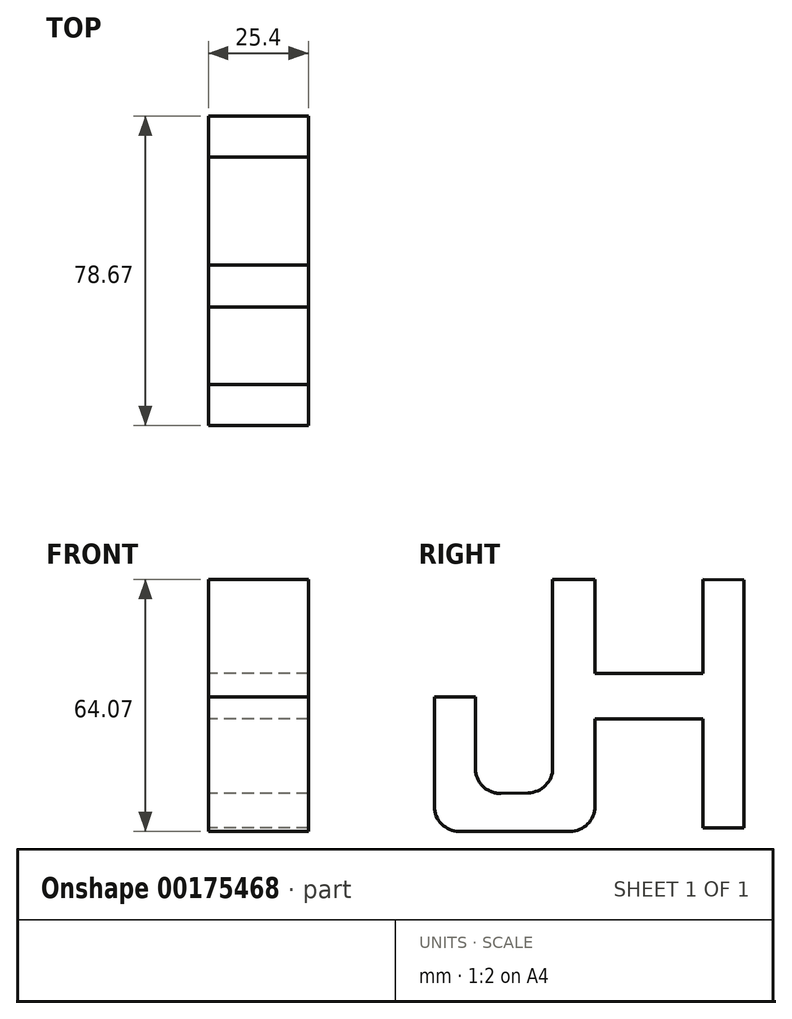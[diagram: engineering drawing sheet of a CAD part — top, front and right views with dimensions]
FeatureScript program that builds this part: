
annotation { "Feature Type Name" : "Feature", "Feature Type Description" : "" }
export const myFeature = defineFeature(function(context is Context, id is Id, definition is map)
    precondition{}
    {
        {
            var Q0;
            Q0=qCreatedBy(makeId("Right.planeOp"),FACE);
            var sketch = newSketch(context, id + "F0", { "sketchPlane" : qUnion([Q0])});
            skLineSegment(sketch, "E0", {"start": v(-25.03, 29.95) * mm, "end": v(-25.03, -17.98) * mm});
            skLineSegment(sketch, "E1", {"start": v(-25.03, 29.95) * mm, "end": v(-14.3, 29.95) * mm});
            skLineSegment(sketch, "E2", {"start": v(-14.3, 29.95) * mm, "end": v(-14.3, -27.77) * mm});
            skLineSegment(sketch, "E3", {"start": v(-20.65, -34.12) * mm, "end": v(-48.78, -34.12) * mm});
            skLineSegment(sketch, "E4", {"start": v(-55.13, -27.77) * mm, "end": v(-55.13, 0) * mm});
            skLineSegment(sketch, "E5", {"start": v(-55.13, 0) * mm, "end": v(-44.7, 0) * mm});
            skLineSegment(sketch, "E6", {"start": v(-44.7, 0) * mm, "end": v(-44.7, -18.12) * mm});
            skLineSegment(sketch, "E7", {"start": v(-38.23, -24.47) * mm, "end": v(-31.26, -24.33) * mm});
            skPoint(sketch, "E8.visualSharp", {"position": v(-44.7, -24.59) * mm});
            skArc(sketch, "E8.filletArc", {"start": v(-44.7, -18.12) * mm, "mid": v(-42.8, -22.65) * mm, "end": v(-38.23, -24.47) * mm});
            skPoint(sketch, "E9.visualSharp", {"position": v(-55.13, -34.12) * mm});
            skArc(sketch, "E9.filletArc", {"start": v(-55.13, -27.77) * mm, "mid": v(-53.27, -32.26) * mm, "end": v(-48.78, -34.12) * mm});
            skPoint(sketch, "E10.visualSharp", {"position": v(-14.3, -34.12) * mm});
            skArc(sketch, "E10.filletArc", {"start": v(-20.65, -34.12) * mm, "mid": v(-16.16, -32.26) * mm, "end": v(-14.3, -27.77) * mm});
            skPoint(sketch, "E11.visualSharp", {"position": v(-25.03, -24.21) * mm});
            skArc(sketch, "E11.filletArc", {"start": v(-31.26, -24.33) * mm, "mid": v(-26.85, -22.43) * mm, "end": v(-25.03, -17.98) * mm});
            skLineSegment(sketch, "E12", {"start": v(-14.3, 6.07) * mm, "end": v(13.11, 6.07) * mm});
            skLineSegment(sketch, "E13", {"start": v(13.11, 29.9) * mm, "end": v(13.11, 29.9) * mm});
            skLineSegment(sketch, "E14", {"start": v(13.11, 29.9) * mm, "end": v(23.54, 29.76) * mm});
            skLineSegment(sketch, "E15", {"start": v(23.54, 29.76) * mm, "end": v(23.54, -33.27) * mm});
            skLineSegment(sketch, "E16", {"start": v(23.54, -33.27) * mm, "end": v(13.11, -33.27) * mm});
            skLineSegment(sketch, "E17", {"start": v(13.11, -33.27) * mm, "end": v(13.11, -5.55) * mm});
            skLineSegment(sketch, "E18", {"start": v(13.11, -5.55) * mm, "end": v(-14.3, -5.55) * mm});
            skLineSegment(sketch, "E19", {"start": v(13.11, 6.07) * mm, "end": v(13.11, 29.9) * mm});
            skSolve(sketch);
        }
        {
            var Q0;
            Q0=makeQuery(id+"F0.imprint","IMPRINT",FACE,{"disambiguationData":[TD([[makeQuery(id+"F0.imprint","IMPRINT",EDGE,{"derivedFrom":sQuery(id+"F0.wireOp",EDGE,"E0")}),1.0]])]});
            extrude(context, id + "F1", {"entities" : qUnion([Q0]), "depth" : 25.4 * mm});
        }
        {
            var Q0;
            Q0 = qSketchRegion(id + "F0", true);
            extrude(context, id + "F2", {"entities" : qUnion([Q0]), "operationType" : NewBodyOperationType.ADD, "depth" : 25.4 * mm});
        }
    });
